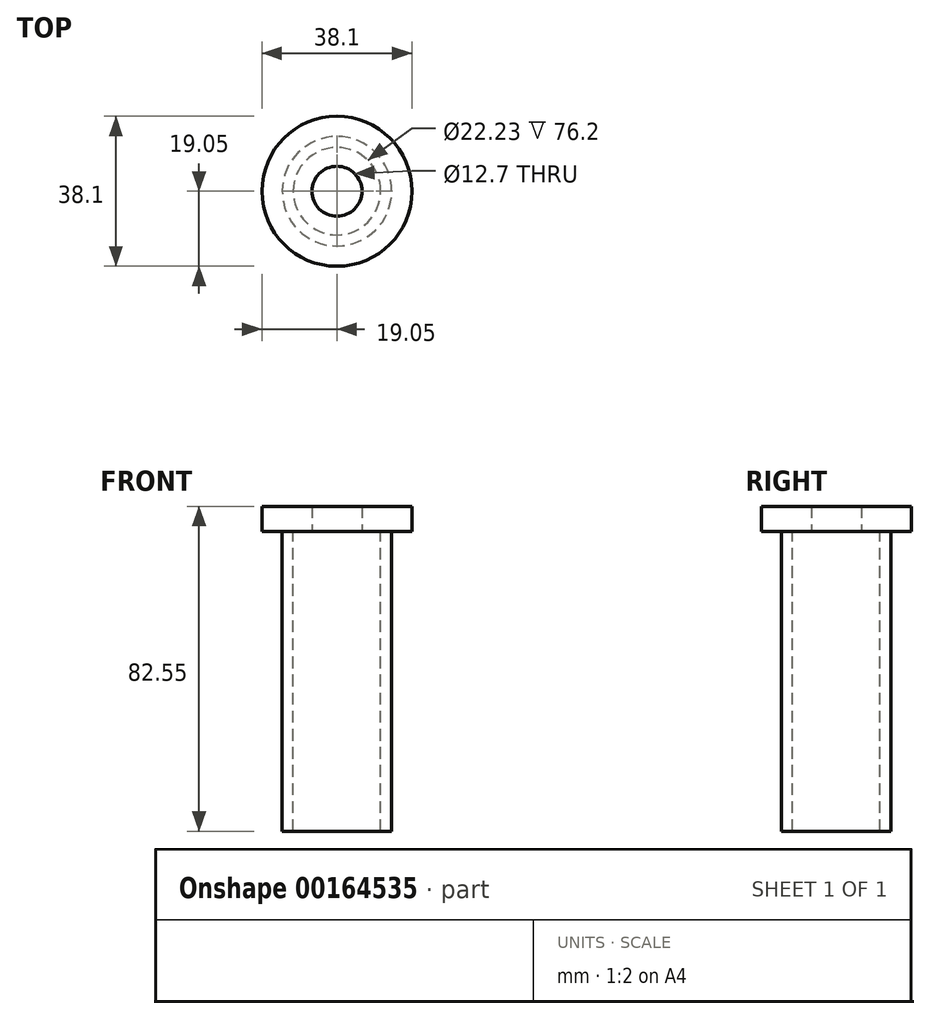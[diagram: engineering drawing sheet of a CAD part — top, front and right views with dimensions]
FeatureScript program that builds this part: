
annotation { "Feature Type Name" : "Feature", "Feature Type Description" : "" }
export const myFeature = defineFeature(function(context is Context, id is Id, definition is map)
    precondition{}
    {
        {
            var Q0;
            Q0=qCreatedBy(makeId("Top.planeOp"),FACE);
            var sketch = newSketch(context, id + "F0", { "sketchPlane" : qUnion([Q0])});
            skCircle(sketch, "E0", {"center": v(0, 0) * mm, "radius": 11.11 * mm});
            skCircle(sketch, "E1", {"center": v(0, 0) * mm, "radius": 13.9 * mm});
            skSolve(sketch);
        }
        {
            var Q0;
            Q0 = qSketchRegion(id + "F0", true);
            extrude(context, id + "F1", {"entities" : qUnion([Q0]), "oppositeDirection" : true, "depth" : 76.2 * mm});
        }
        {
            var Q0;
            Q0=qCreatedBy(makeId("Top.planeOp"),FACE);
            var sketch = newSketch(context, id + "F2", { "sketchPlane" : qUnion([Q0])});
            skCircle(sketch, "E2", {"center": v(0, 0) * mm, "radius": 6.35 * mm});
            skCircle(sketch, "E3", {"center": v(0, 0) * mm, "radius": 19.05 * mm});
            skSolve(sketch);
        }
        {
            var Q0;
            Q0 = qSketchRegion(id + "F2", true);
            extrude(context, id + "F3", {"entities" : qUnion([Q0]), "operationType" : NewBodyOperationType.ADD, "depth" : 6.35 * mm});
        }
    });
